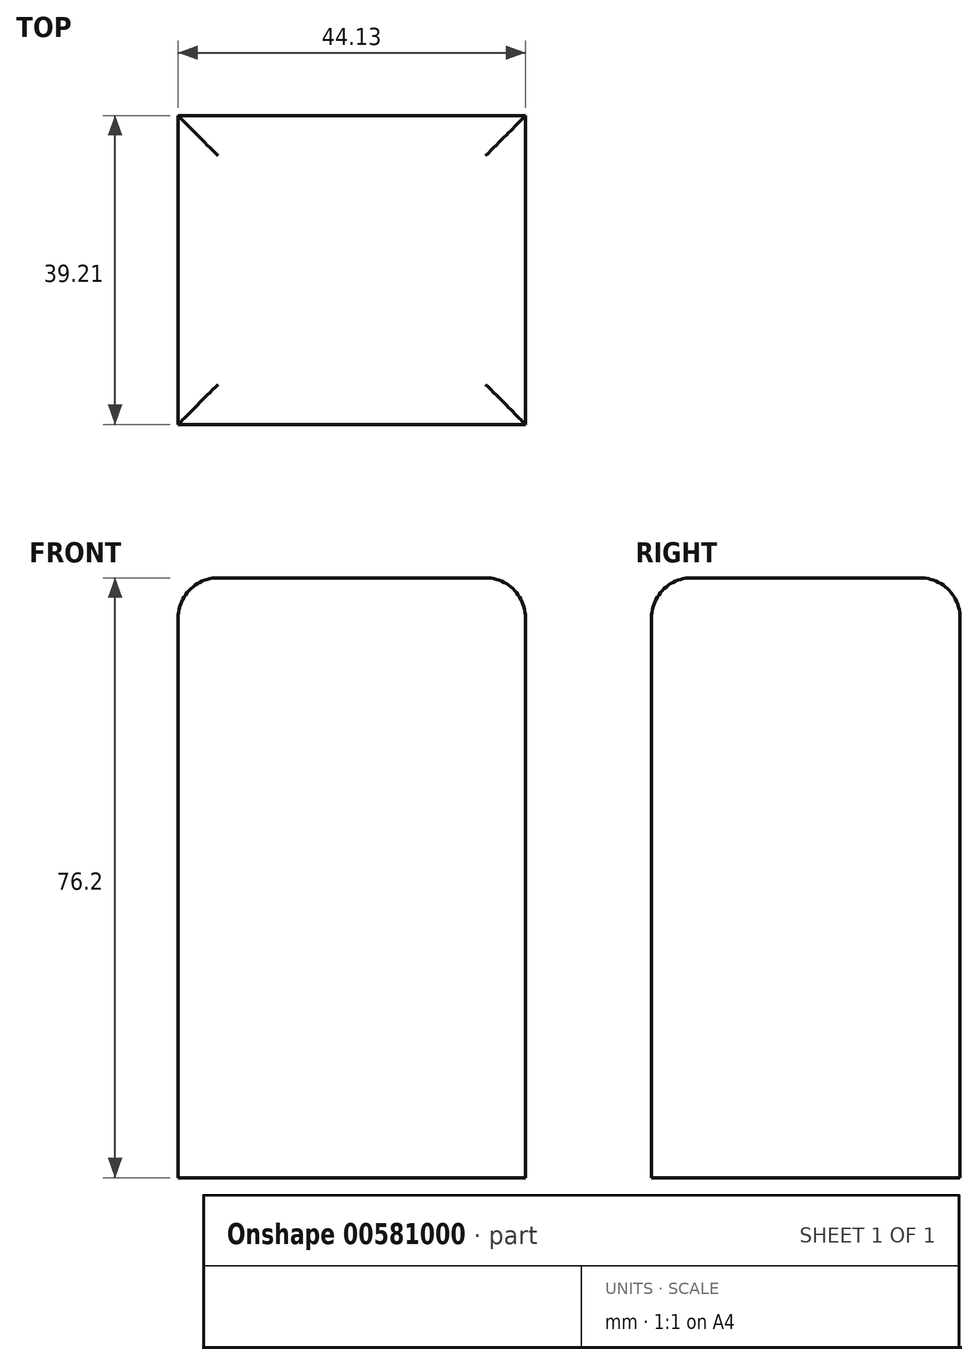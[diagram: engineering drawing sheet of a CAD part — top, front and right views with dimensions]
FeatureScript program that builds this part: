
annotation { "Feature Type Name" : "Feature", "Feature Type Description" : "" }
export const myFeature = defineFeature(function(context is Context, id is Id, definition is map)
    precondition{}
    {
        {
            var Q0;
            Q0=qCreatedBy(makeId("Top.planeOp"),FACE);
            var sketch = newSketch(context, id + "F0", { "sketchPlane" : qUnion([Q0])});
            skLineSegment(sketch, "E0.bottom", {"start": v(0, 0) * mm, "end": v(44.13, 0) * mm});
            skLineSegment(sketch, "E0.top", {"start": v(0, 39.2) * mm, "end": v(44.13, 39.2) * mm});
            skLineSegment(sketch, "E0.left", {"start": v(0, 0) * mm, "end": v(0, 39.2) * mm});
            skLineSegment(sketch, "E0.right", {"start": v(44.13, 0) * mm, "end": v(44.13, 39.2) * mm});
            skSolve(sketch);
        }
        {
            var Q0;
            Q0 = qSketchRegion(id + "F0", true);
            extrude(context, id + "F1", {"entities" : qUnion([Q0]), "depth" : 76.2 * mm, "offsetDistance" : 25.4 * mm});
        }
        {
            var Q0;
            Q0=makeQuery(id+"F1.opExtrude","CAP_EDGE",EDGE,{"disambiguationData":[OSD([sQuery(id+"F0.wireOp",EDGE,"E0.top")])],"isStart":false});
            var Q1;
            Q1=makeQuery(id+"F1.opExtrude","CAP_EDGE",EDGE,{"disambiguationData":[OSD([sQuery(id+"F0.wireOp",EDGE,"E0.right")])],"isStart":false});
            var Q2;
            Q2=makeQuery(id+"F1.opExtrude","CAP_FACE",FACE,{"disambiguationData":[OSD([sQuery(id+"F0.wireOp",EDGE,"E0.bottom"),sQuery(id+"F0.wireOp",EDGE,"E0.top"),sQuery(id+"F0.wireOp",EDGE,"E0.left"),sQuery(id+"F0.wireOp",EDGE,"E0.right")])],"isStart":false});
            fillet(context, id + "F2", {"entities" : qUnion([Q0, Q1, Q2]), "radius" : 5.08 * mm, "tangentPropagation" : true, "allowEdgeOverflow" : false});
        }
    });
